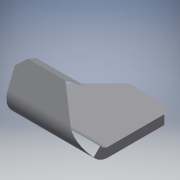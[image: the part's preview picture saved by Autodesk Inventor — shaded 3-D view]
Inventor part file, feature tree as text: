
AUTODESK INVENTOR PART (.ipt)
format: ipt  version: 2016 (Build 200138000, 138)  size: 119,808 bytes
history: native  units: mm
features: sheet_metal_op x4, other x3, sketch x2
ambient origin geometry x8: Origin, YZ Plane, XZ Plane, XY Plane, X Axis, Y Axis, Z Axis, Center Point
bodies: Solid1 (feature_tree)
feature tree (9):
  sheet_metal_op  "Face1"
  sheet_metal_op  "Flange1"
  other  "Corner Chamfer1"
  sketch  "Sketch1"  dims[d0=18.0mm]
  other  "Plate1"
  sketch  "Sketch2"  dims[d1=20.0mm d2=2.0mm d3=2.0mm d4=1.0mm d5=4.0mm d6=2.0mm d7=12.0mm d8=19.540706mm d9=2.0mm d10=8.0mm d11=2.0mm d12=2.0mm d13=2.0mm d14=6.0mm d15=45.0deg]
  other  "Plate2"
  sheet_metal_op  "Bend1"
  sheet_metal_op  "Corner1"
